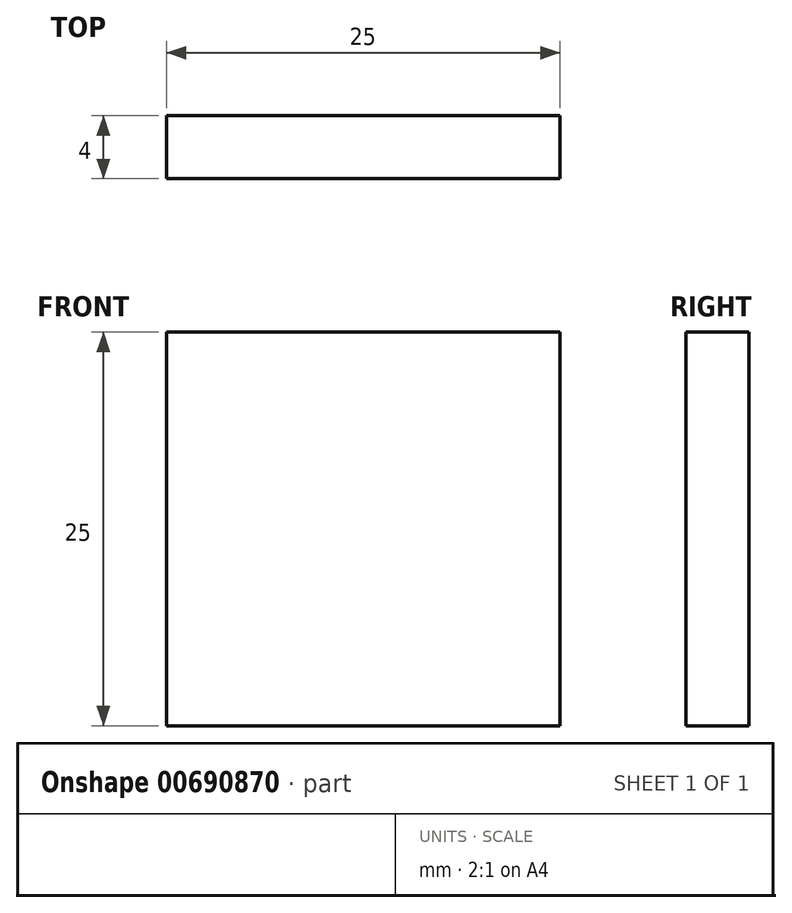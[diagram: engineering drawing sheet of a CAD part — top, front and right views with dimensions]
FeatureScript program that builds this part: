
annotation { "Feature Type Name" : "Feature", "Feature Type Description" : "" }
export const myFeature = defineFeature(function(context is Context, id is Id, definition is map)
    precondition{}
    {
        {
            var Q0;
            Q0=qCreatedBy(makeId("Front.planeOp"),FACE);
            var sketch = newSketch(context, id + "F0", { "sketchPlane" : qUnion([Q0])});
            skLineSegment(sketch, "E0.bottom", {"start": v(12.5, 12.5) * mm, "end": v(-12.5, 12.5) * mm});
            skLineSegment(sketch, "E0.top", {"start": v(12.5, -12.5) * mm, "end": v(-12.5, -12.5) * mm});
            skLineSegment(sketch, "E0.left", {"start": v(12.5, 12.5) * mm, "end": v(12.5, -12.5) * mm});
            skLineSegment(sketch, "E0.right", {"start": v(-12.5, 12.5) * mm, "end": v(-12.5, -12.5) * mm});
            skPoint(sketch, "E0.middle", {"position": v(0, 0) * mm});
            skSolve(sketch);
        }
        {
            var Q0;
            Q0 = qSketchRegion(id + "F0", true);
            extrude(context, id + "F1", {"entities" : qUnion([Q0]), "depth" : 4 * mm, "offsetDistance" : 25 * mm});
        }
    });
